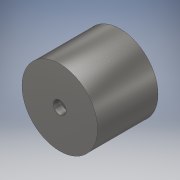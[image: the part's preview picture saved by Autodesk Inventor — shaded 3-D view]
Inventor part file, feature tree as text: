
AUTODESK INVENTOR PART (.ipt)
format: ipt  version: 2018.3 (Build 223284000, 284)  size: 122,880 bytes
history: native  units: mm
features: sketch x2, revolve x1, hole x1
ambient origin geometry x8: Origin, YZ Plane, XZ Plane, XY Plane, X Axis, Y Axis, Z Axis, Center Point
bodies: Volumenkörper1 (feature_tree)
feature tree (4):
  revolve  "Umdrehung1"
  hole  "Bohrung1"  [1 undecoded]
  sketch  "Skizze1"  dims[d0=10.0mm d1=25.0mm]
  sketch  "Skizze2"  dims[d2=10.0mm d3=90.0deg d4=8.5mm d5=6.0mm d6=4.0mm d7=2.0mm d8=90.0deg d9=8.0mm d10=20.594885mm d11=5.0mm d12=40.0mm]
note: 1 required parameter value undecoded (feature->parameter linkage not recoverable at this tier; creation-order binding heuristic only, values carry confidence <= 0.55)
